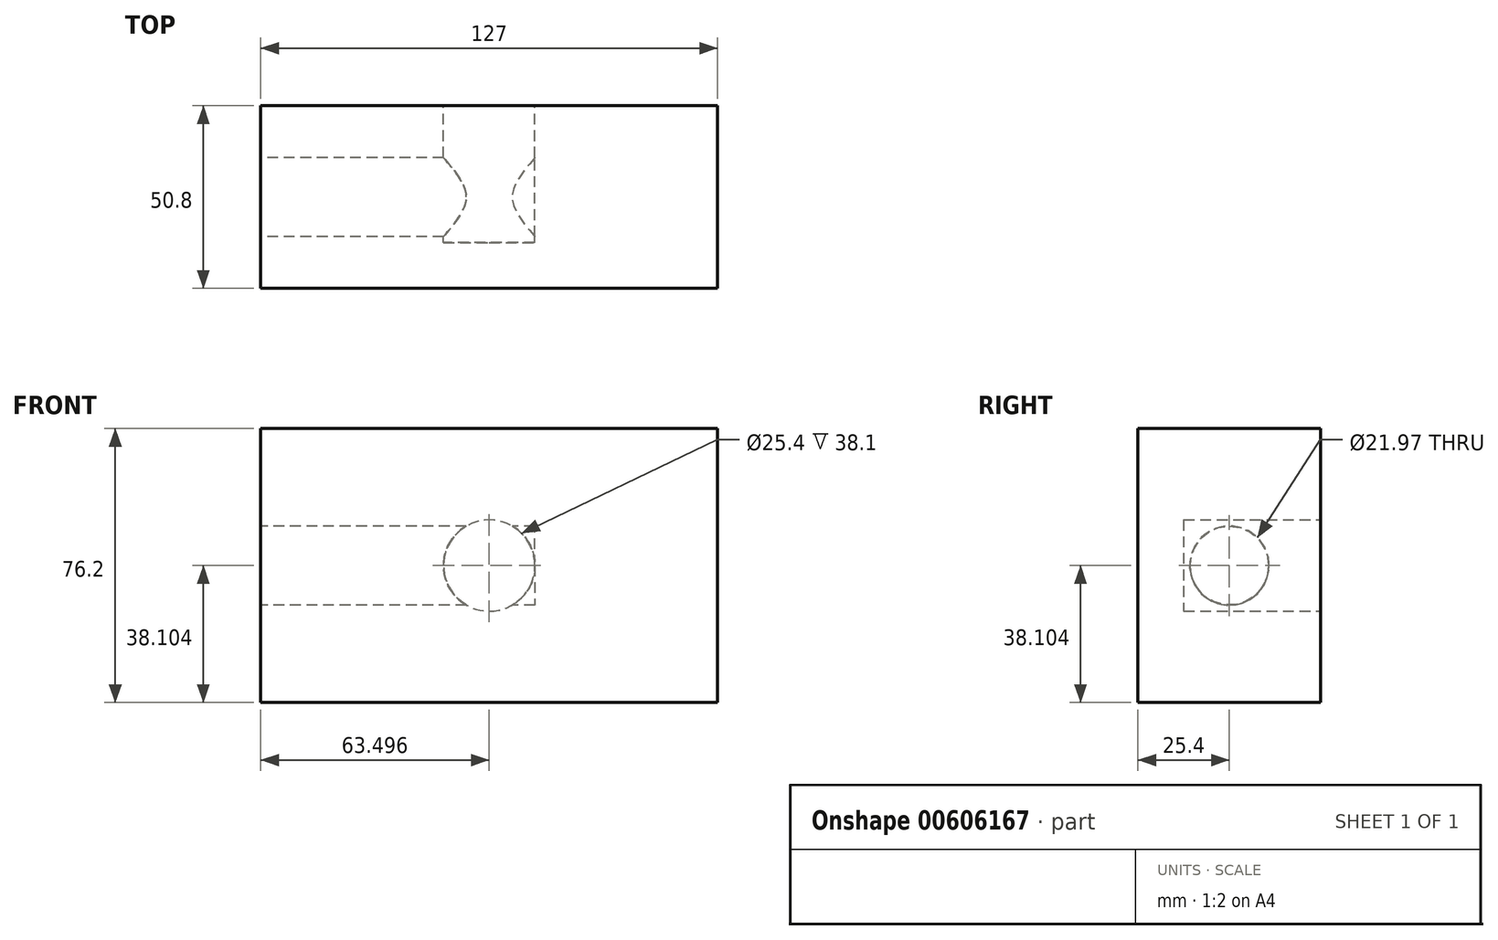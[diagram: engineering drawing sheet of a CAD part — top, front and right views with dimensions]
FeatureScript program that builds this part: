
annotation { "Feature Type Name" : "Feature", "Feature Type Description" : "" }
export const myFeature = defineFeature(function(context is Context, id is Id, definition is map)
    precondition{}
    {
        {
            var Q0;
            Q0=qCreatedBy(makeId("Front.planeOp"),FACE);
            var sketch = newSketch(context, id + "F0", { "sketchPlane" : qUnion([Q0])});
            skLineSegment(sketch, "E0.bottom", {"start": v(-59.62, 14.71) * mm, "end": v(67.38, 14.71) * mm});
            skLineSegment(sketch, "E0.top", {"start": v(-59.62, -61.49) * mm, "end": v(67.38, -61.49) * mm});
            skLineSegment(sketch, "E0.left", {"start": v(-59.62, 14.71) * mm, "end": v(-59.62, -61.49) * mm});
            skLineSegment(sketch, "E0.right", {"start": v(67.38, 14.71) * mm, "end": v(67.38, -61.49) * mm});
            skLineSegment(sketch, "E1.left", {"start": v(-59.62, 0) * mm, "end": v(-59.62, 0) * mm});
            skSolve(sketch);
        }
        {
            var Q0;
            Q0=makeQuery(id+"F0.imprint","IMPRINT",FACE,{"disambiguationData":[TD([[makeQuery(id+"F0.imprint","IMPRINT",EDGE,{"derivedFrom":sQuery(id+"F0.wireOp",EDGE,"E0.bottom")}),-1.0]])]});
            extrude(context, id + "F1", {"entities" : qUnion([Q0]), "depth" : 50.8 * mm, "offsetDistance" : 25.4 * mm});
        }
        {
            var Q0;
            Q0=makeQuery(id+"F1.opExtrude","CAP_FACE",FACE,{"disambiguationData":[OSD([sQuery(id+"F0.wireOp",EDGE,"E0.bottom"),sQuery(id+"F0.wireOp",EDGE,"E0.top"),sQuery(id+"F0.wireOp",EDGE,"E0.left"),sQuery(id+"F0.wireOp",EDGE,"E0.right")])],"isStart":true});
            var sketch = newSketch(context, id + "F2", { "sketchPlane" : qUnion([Q0])});
            skCircle(sketch, "E2", {"center": v(-3.88, -23.39) * mm, "radius": 12.7 * mm});
            skSolve(sketch);
        }
        {
            var Q0;
            Q0=makeQuery(id+"F2.imprint","IMPRINT",FACE,{"disambiguationData":[TD([[makeQuery(id+"F2.imprint","IMPRINT",EDGE,{"derivedFrom":sQuery(id+"F2.wireOp",EDGE,"E2")}),1.0]])]});
            extrude(context, id + "F3", {"entities" : qUnion([Q0]), "operationType" : NewBodyOperationType.REMOVE, "oppositeDirection" : true, "depth" : 38.1 * mm, "offsetDistance" : 25.4 * mm});
        }
        {
            var Q0;
            Q0=makeQuery(id+"F1.opExtrude","SWEPT_FACE",FACE,{"disambiguationData":[OSD([sQuery(id+"F0.wireOp",EDGE,"E0.left")])]});
            var sketch = newSketch(context, id + "F4", { "sketchPlane" : qUnion([Q0])});
            skCircle(sketch, "E3", {"center": v(25.4, -23.39) * mm, "radius": 10.98 * mm});
            skSolve(sketch);
        }
        {
            var Q0;
            Q0=makeQuery(id+"F4.imprint","IMPRINT",FACE,{"disambiguationData":[TD([[makeQuery(id+"F4.imprint","IMPRINT",EDGE,{"derivedFrom":sQuery(id+"F4.wireOp",EDGE,"E3")}),1.0]])]});
            extrude(context, id + "F5", {"entities" : qUnion([Q0]), "operationType" : NewBodyOperationType.REMOVE, "oppositeDirection" : true, "depth" : 76.2 * mm, "offsetDistance" : 25.4 * mm});
        }
    });
